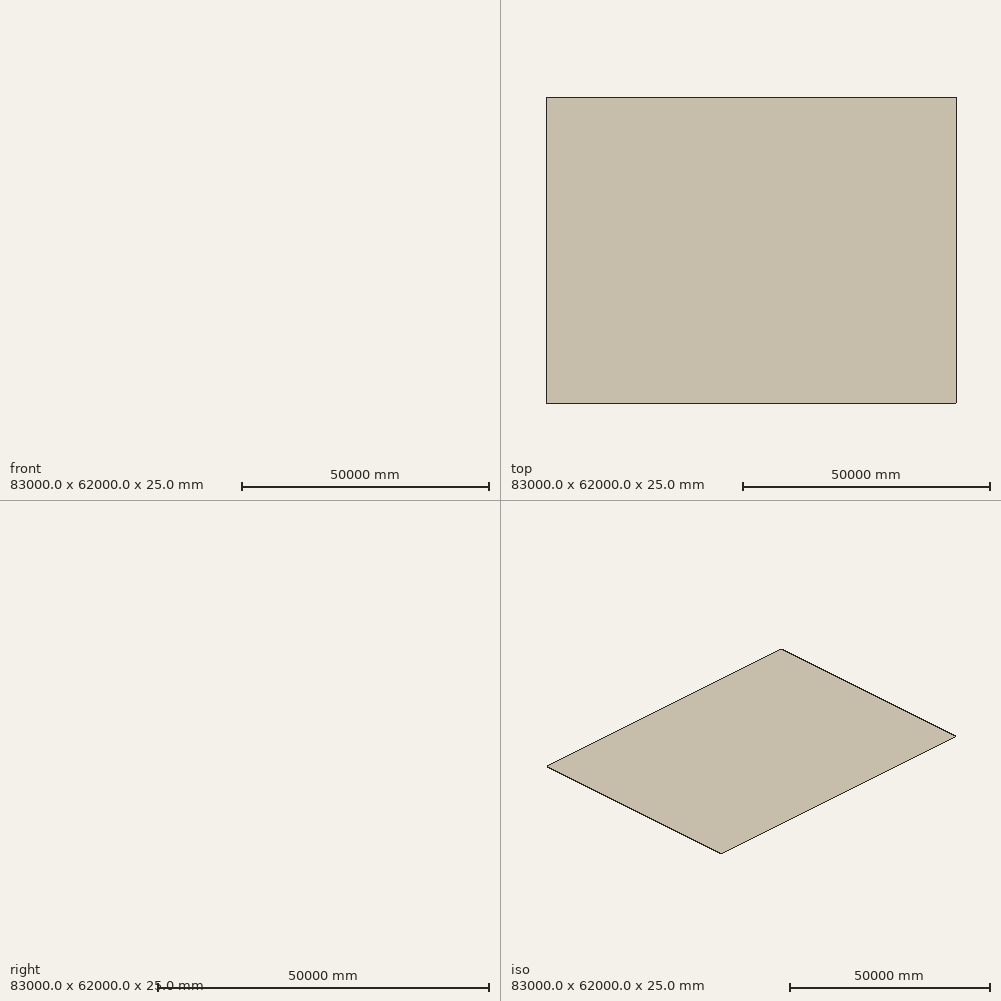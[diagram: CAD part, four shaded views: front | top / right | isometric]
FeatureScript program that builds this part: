
annotation { "Feature Type Name" : "Feature", "Feature Type Description" : "" }
export const myFeature = defineFeature(function(context is Context, id is Id, definition is map)
    precondition{}
    {
        {
            var Q0;
            Q0=qCreatedBy(makeId("Top.planeOp"),FACE);
            var sketch = newSketch(context, id + "F0", { "sketchPlane" : qUnion([Q0])});
            skLineSegment(sketch, "E0.bottom", {"start": v(-41500, 31000) * mm, "end": v(41500, 31000) * mm});
            skLineSegment(sketch, "E0.top", {"start": v(-41500, -31000) * mm, "end": v(41500, -31000) * mm});
            skLineSegment(sketch, "E0.left", {"start": v(-41500, 31000) * mm, "end": v(-41500, -31000) * mm});
            skLineSegment(sketch, "E0.right", {"start": v(41500, 31000) * mm, "end": v(41500, -31000) * mm});
            skPoint(sketch, "E0.middle", {"position": v(0, 0) * mm});
            skPoint(sketch, "E1", {"position": v(-39300, 28800) * mm});
            skPoint(sketch, "E2", {"position": v(-35100, 28800) * mm});
            skPoint(sketch, "E3", {"position": v(-30900, 28800) * mm});
            skPoint(sketch, "E4", {"position": v(-26700, 28800) * mm});
            skPoint(sketch, "E5", {"position": v(-22500, 28800) * mm});
            skPoint(sketch, "E6", {"position": v(-18300, 28800) * mm});
            skPoint(sketch, "E7", {"position": v(-14100, 28800) * mm});
            skPoint(sketch, "E8", {"position": v(-9900, 28800) * mm});
            skPoint(sketch, "E9", {"position": v(-5700, 28800) * mm});
            skPoint(sketch, "E10", {"position": v(-1500, 28800) * mm});
            skPoint(sketch, "E11", {"position": v(2700, 28800) * mm});
            skPoint(sketch, "E12", {"position": v(6900, 28800) * mm});
            skPoint(sketch, "E13", {"position": v(11100, 28800) * mm});
            skPoint(sketch, "E14", {"position": v(15300, 28800) * mm});
            skPoint(sketch, "E15", {"position": v(19500, 28800) * mm});
            skPoint(sketch, "E16", {"position": v(23700, 28800) * mm});
            skPoint(sketch, "E17", {"position": v(27900, 28800) * mm});
            skPoint(sketch, "E18", {"position": v(32100, 28800) * mm});
            skPoint(sketch, "E19", {"position": v(36300, 28800) * mm});
            skSolve(sketch);
        }
        {
            var Q0;
            Q0=makeQuery(id+"F0.imprint","IMPRINT",FACE,{"disambiguationData":[TD([[makeQuery(id+"F0.imprint","IMPRINT",EDGE,{"derivedFrom":sQuery(id+"F0.wireOp",EDGE,"E0.bottom")}),-1.0]])]});
            extrude(context, id + "F1", {"entities" : qUnion([Q0]), "depth" : 25 * mm, "offsetDistance" : 25 * mm});
        }
        {
            var Q0;
            Q0=sQuery(id+"F0.wireOp",VERTEX,"E19");
            var Q1;
            Q1=sQuery(id+"F0.wireOp",VERTEX,"E18");
            var Q2;
            Q2=sQuery(id+"F0.wireOp",VERTEX,"E17");
            var Q3;
            Q3=sQuery(id+"F0.wireOp",VERTEX,"E16");
            var Q4;
            Q4=sQuery(id+"F0.wireOp",VERTEX,"E15");
            var Q5;
            Q5=sQuery(id+"F0.wireOp",VERTEX,"E14");
            var Q6;
            Q6=sQuery(id+"F0.wireOp",VERTEX,"E13");
            var Q7;
            Q7=sQuery(id+"F0.wireOp",VERTEX,"E12");
            var Q8;
            Q8=sQuery(id+"F0.wireOp",VERTEX,"E11");
            var Q9;
            Q9=sQuery(id+"F0.wireOp",VERTEX,"E10");
            var Q10;
            Q10=sQuery(id+"F0.wireOp",VERTEX,"E9");
            var Q11;
            Q11=sQuery(id+"F0.wireOp",VERTEX,"E8");
            var Q12;
            Q12=sQuery(id+"F0.wireOp",VERTEX,"E7");
            var Q13;
            Q13=sQuery(id+"F0.wireOp",VERTEX,"E6");
            var Q14;
            Q14=sQuery(id+"F0.wireOp",VERTEX,"E5");
            var Q15;
            Q15=sQuery(id+"F0.wireOp",VERTEX,"E4");
            var Q16;
            Q16=sQuery(id+"F0.wireOp",VERTEX,"E3");
            var Q17;
            Q17=sQuery(id+"F0.wireOp",VERTEX,"E2");
            var Q18;
            Q18=sQuery(id+"F0.wireOp",VERTEX,"E1");
            var Q19;
            Q19=makeQuery(id+"F1.opExtrude","SWEPT_BODY",BODY,{"disambiguationData":[OSD([sQuery(id+"F0.wireOp",EDGE,"E0.bottom"),sQuery(id+"F0.wireOp",EDGE,"E0.top"),sQuery(id+"F0.wireOp",EDGE,"E0.left"),sQuery(id+"F0.wireOp",EDGE,"E0.right")])]});
            hole(context, id + "F2", {"style" : HoleStyle.SIMPLE, "endStyle" : HoleEndStyle.BLIND, "oppositeDirection" : true, "holeDiameter" : 50 * mm, "majorDiameter" : 5 * mm, "holeDepth" : 50 * mm, "isTappedThrough" : true, "tappedDepth" : 12 * mm, "tapClearance" : 3, "startFromSketch" : true, "locations" : qUnion([Q0, Q1, Q2, Q3, Q4, Q5, Q6, Q7, Q8, Q9, Q10, Q11, Q12, Q13, Q14, Q15, Q16, Q17, Q18]), "scope" : qUnion([Q19])});
        }
    });
